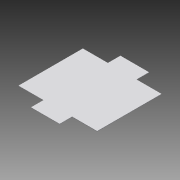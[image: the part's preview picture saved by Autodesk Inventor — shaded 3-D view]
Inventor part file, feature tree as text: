
AUTODESK INVENTOR PART (.ipt)
format: ipt  version: 2014 SP1 (Build 180222100, 222)  size: 82,944 bytes
history: native  units: in
note: dims shown in document units (in); Inventor stores cm internally (conversion verified against a paired STEP export)
features: extrude x1, sketch x1
ambient origin geometry x8: Origin, YZ Plane, XZ Plane, XY Plane, X Axis, Y Axis, Z Axis, Center Point
bodies: Solid1 (feature_tree)
feature tree (2):
  extrude  "Extrusion1"  Depth=7.0in
  sketch  "Sketch1"  dims[d0=3.5in d1=7.0in d2=3.5in d3=7.0in d4=7.0in d5=3.5in d6=7.0in d7=3.5in d8=22.0in d9=25.0in d10=0.125in d11=0.0in]
